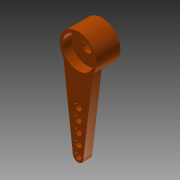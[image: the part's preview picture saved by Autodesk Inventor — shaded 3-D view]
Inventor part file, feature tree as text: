
AUTODESK INVENTOR PART (.ipt)
format: ipt  version: 2015 (Build 190159000, 159)  size: 126,464 bytes
history: native  units: mm
features: extrude x4, sketch x3, projected_geometry x1
ambient origin geometry x8: Origin, YZ Plane, XZ Plane, XY Plane, X Axis, Y Axis, Z Axis, Center Point
bodies: Solid1 (feature_tree)
feature tree (8):
  sketch  "Sketch1"  dims[d2=2.22mm d3=0.629449mm]
  extrude  "Extrusion1"  Depth=0.629449mm
  extrude  "Extrusion2"  Depth=0.63mm TaperAngle=0.0deg
  extrude  "Extrusion3"  Depth=2.06mm
  extrude  "Extrusion4"  Depth=2.06mm
  sketch  "Sketch2"  dims[d4=2.07mm d5=0.0mm d6=0.63mm d7=0.0mm]
  projected_geometry  "Projected Loop1"
  sketch  "Sketch3"  dims[d8=2.81mm d9=0.0mm d14=1.5mm d15=0.46mm d16=1.5mm d17=0.95mm d18=1.5mm d19=1.5mm d20=1.5mm d21=0.95mm d22=0.95mm d23=0.95mm d24=2.06mm d25=0.0mm d26=4.75mm]
